# Revit family: Orbit
name_source: partatom
category: Mechanical Equipment
units: mm (PartAtom-declared; Revit-internal decimal feet)

## family parameters
Always vertical = No
Classification = None
Cut with Voids When Loaded = No
OmniClass Number = 23.75.00.00
OmniClass Title = Climate Control (HVAC)
Part Type = Normal
Room Calculation Point = No
Round Connector Dimension = Use Diameter
Shared = No
Work Plane-Based = Yes

## types (1)
- Orbit
    Communication ID = 0
    Connection cable = (STP) 2x2x0.6 data cable
    Default Elevation = 1219 mm
    Depth = 12 mm  [stored 0.0393701 ft]
    Description = Control Panel for Airmaster units
    Group ID = 0 mm  [stored 0 ft]
    Hight = 82 mm  [stored 0.269029 ft]
    Manufacturer = Airmaster A/S
    Model = Orbit Panel
    URL = https://www.airmaster-as.com
    With = 82 mm  [stored 0.269029 ft]

note: [stored X ft] marks values corroborated as IEEE doubles in the binary element streams (Revit-internal decimal feet)

## geometry (parser evidence)
native form markers: Sweep x3
no freeform markers — native parametric forms only
